# Revit family: 1Drinking_Fountain-Haws_Corporation-Wall_Mounted_2000
name_source: partatom
category: Plumbing Fixtures
units: mm (PartAtom-declared; Revit-internal decimal feet)

## family parameters
Always vertical = Yes
Cut with Voids When Loaded = No
Host = Wall
Maintain Annotation Orientation = No
OmniClass Number = 23.65.70.14.11
OmniClass Title = Drinking Fountains/Coolers
Part Type = Normal
Room Calculation Point = No
Round Connector Dimension = Use Radius
Shared = Yes

## types (4) — shared parameters
Apparent Load = 1800 VA
Assembly Code = D2010810
Back Panel = Metal - Haws Corporation - Satin Stainless Steel
CW Connection = No
CWFU = 1
Cost = $0
Current = 15 A
Default Elevation = 27"
Flow = 0.00 GPM
HS Void Depth = 4"
HW Connection = No
Hs Void Height = 16 3/8"
Hs Void Width = 12"
Keynote = 15410.A1
Manufacturer = Haws Corporation
Number of Poles = 1
Pipe Offset = 12 1/2"
Power Factor = 1
Product Documentation Link = https://www.hawsco.com
Product Page URL = https://www.hawsco.com
Sanitary Radius = 5/8"
Series = The Haws 2000 surface-mounted bottle filler
Supply Radius = 3/16"
Tubing = Metal - Haws Corporation - Copper Poly
Type Comments = Placed securely in multiple locations without taking up excess space
URL = http://www.hawsco.com
Vent Connection = Yes
Version = 1
Voltage = 120 V
Waste Connection = No
Waste Level = 28 3/32"

## per-type parameters (varying)
| type | All Connectors | Bottom Panel Height | Bowl Diameter | Chiller Connectors | Chiller Void Bottom | Chiller Void L/R | Chiller Void Top | Chiller and Grille | Cold Water Offset | Description | HSSM | Model | No Chiller Connector | Panel Depth Offset | Panel Offset | Plate Height | Product data url |
| 2000HS | No | 9" | 17 1/4" | 2 | 28 3/32" | 5/32" | 28 5/32" | No | 1 7/8" | Model 2000HS features an architectural designed recessed bottle filler, field configurable filtration, a sensor-operated 1.2 gpm fill rate, and auto-purge functionality. | No | 2000HS | 3 | 1/2" | 1 3/8" | 28 3/8" | https://www.bimobject.com |
| 2000HSA.8 | No | 21 5/8" | 19 5/8" | 3 | 4" | 6 5/8" | 21 5/16" | Yes | 0" | Model 2000HSA.8 features a chilled architectural designed recessed bottle filler, field configurable filtration, a sensor-operated 1.1 gpm fill rate, energy-saving features, and auto-purge functionality. | No | 2000HSA.8 | 2 | 1/2" | 1 7/8" | 28 3/8" | https://www.bimobject.com |
| 2000HSSM | No | 9" | 17 1/4" | 2 | 28 3/32" | 5/32" | 28 5/32" | No | 1 7/8" | Model 2000HSSM features an architectural designed surface-mounted bottle filler with field configurable filtration, a sensor-operated 1.2 gpm fill rate, and auto-purge functionality. | Yes | 2000HSSM | 3 | 4 1/2" | 5 3/8" | 30 3/4" | https://www.bimobject.com |
| Default - please remove it after downloading it | Yes | 9" | 17 1/4" | 3 | 28 3/32" | 5/32" | 28 5/32" | No | 1 7/8" | Model 2000HS features an architectural designed recessed bottle filler, field configurable filtration, a sensor-operated 1.2 gpm fill rate, and auto-purge functionality. | No | 2000HS | 3 | 1/2" | 1 3/8" | 28 3/8" |  |

## geometry (parser evidence)
native form markers: Sweep x8
no freeform markers — native parametric forms only
